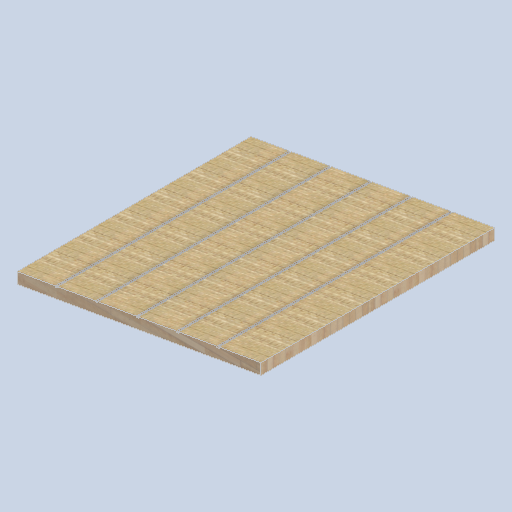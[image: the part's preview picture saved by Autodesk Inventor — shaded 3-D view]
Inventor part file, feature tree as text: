
AUTODESK INVENTOR PART (.ipt)
format: ipt  version: 2024.2 (Build 282272000, 272)  size: 253,440 bytes
history: native  units: in
note: dims shown in document units (in); Inventor stores cm internally (conversion verified against a paired STEP export)
features: sketch x4, other x3, plane x3
ambient origin geometry x8: Origin, YZ Plane, XZ Plane, XY Plane, X Axis, Y Axis, Z Axis, Center Point
bodies: Solid1 (feature_tree)
feature tree (10):
  other  "eave_panel_side_MIR.ipt"
  other  "Solid1::eave_panel_side_MIR.ipt"
  other  "TaggingFeature1"
  sketch  "Sketch1"  dims[d0=0.3937in]
  sketch  "Sketch2"
  sketch  "Sketch3"
  sketch  "Sketch4"
  plane  "Work Plane1"
  plane  "Work Plane2"
  plane  "Work Plane3"
